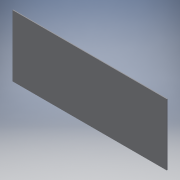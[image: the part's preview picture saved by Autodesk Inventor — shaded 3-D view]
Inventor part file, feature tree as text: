
AUTODESK INVENTOR PART (.ipt)
format: ipt  version: 2019 (Build 230136000, 136)  size: 89,088 bytes
history: native  units: mm
features: extrude x1, sketch x1
ambient origin geometry x8: Origin, YZ Plane, XZ Plane, XY Plane, X Axis, Y Axis, Z Axis, Center Point
bodies: Solid1 (feature_tree)
feature tree (2):
  extrude  "Extrusion1"  Depth=800.0mm
  sketch  "Sketch1"  dims[d0=2000.0mm d1=800.0mm d2=10.0mm d3=0.0mm]
